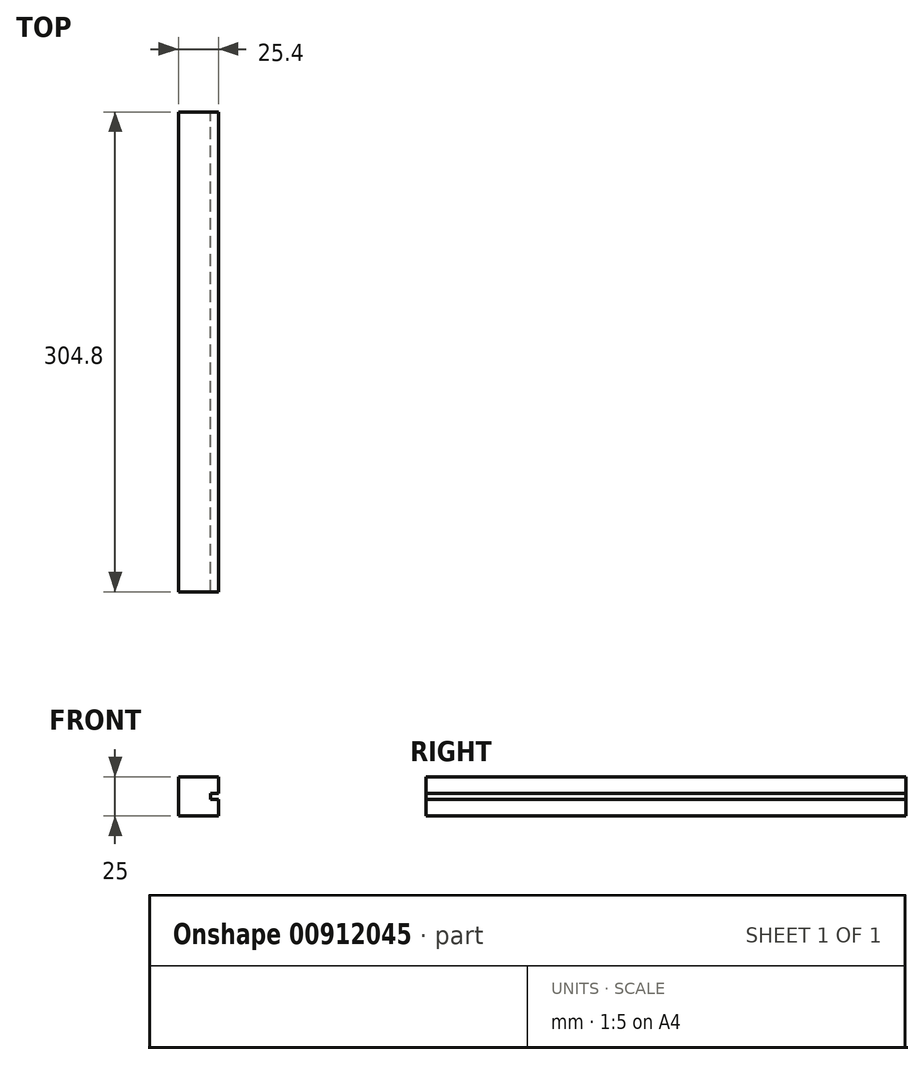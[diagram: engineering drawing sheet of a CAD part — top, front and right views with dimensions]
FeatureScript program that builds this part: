
annotation { "Feature Type Name" : "Feature", "Feature Type Description" : "" }
export const myFeature = defineFeature(function(context is Context, id is Id, definition is map)
    precondition{}
    {
        {
            var Q0;
            Q0=qCreatedBy(makeId("Top.planeOp"),FACE);
            var sketch = newSketch(context, id + "F0", { "sketchPlane" : qUnion([Q0])});
            skLineSegment(sketch, "E0.bottom", {"start": v(-54.85, 213.34) * mm, "end": v(-29.45, 213.34) * mm});
            skLineSegment(sketch, "E0.top", {"start": v(-54.85, -91.46) * mm, "end": v(-29.45, -91.46) * mm});
            skLineSegment(sketch, "E0.left", {"start": v(-54.85, 213.34) * mm, "end": v(-54.85, -91.46) * mm});
            skLineSegment(sketch, "E0.right", {"start": v(-29.45, 213.34) * mm, "end": v(-29.45, -91.46) * mm});
            skSolve(sketch);
        }
        {
            var Q0;
            Q0=makeQuery(id+"F0.imprint","IMPRINT",FACE,{"disambiguationData":[TD([[makeQuery(id+"F0.imprint","IMPRINT",EDGE,{"derivedFrom":sQuery(id+"F0.wireOp",EDGE,"E0.bottom")}),-1.0]])]});
            extrude(context, id + "F1", {"entities" : qUnion([Q0]), "depth" : 25 * mm, "offsetDistance" : 25 * mm});
        }
        {
            var Q0;
            Q0=makeQuery(id+"F1.opExtrude","SWEPT_FACE",FACE,{"disambiguationData":[OSD([sQuery(id+"F0.wireOp",EDGE,"E0.right")])]});
            var sketch = newSketch(context, id + "F2", { "sketchPlane" : qUnion([Q0])});
            skLineSegment(sketch, "E1.bottom", {"start": v(-91.46, 14.5) * mm, "end": v(213.34, 14.5) * mm});
            skLineSegment(sketch, "E1.top", {"start": v(-91.46, 10.5) * mm, "end": v(213.34, 10.5) * mm});
            skLineSegment(sketch, "E1.left", {"start": v(-91.46, 14.5) * mm, "end": v(-91.46, 10.5) * mm});
            skLineSegment(sketch, "E1.right", {"start": v(213.34, 14.5) * mm, "end": v(213.34, 10.5) * mm});
            skPoint(sketch, "E2", {"position": v(-91.46, 12.5) * mm});
            skSolve(sketch);
        }
        {
            var Q0;
            Q0=makeQuery(id+"F2.imprint","IMPRINT",FACE,{"disambiguationData":[TD([[makeQuery(id+"F2.imprint","IMPRINT",EDGE,{"derivedFrom":sQuery(id+"F2.wireOp",EDGE,"E1.bottom")}),-1.0]])]});
            extrude(context, id + "F3", {"entities" : qUnion([Q0]), "operationType" : NewBodyOperationType.REMOVE, "oppositeDirection" : true, "depth" : 5 * mm, "offsetDistance" : 25 * mm});
        }
    });
